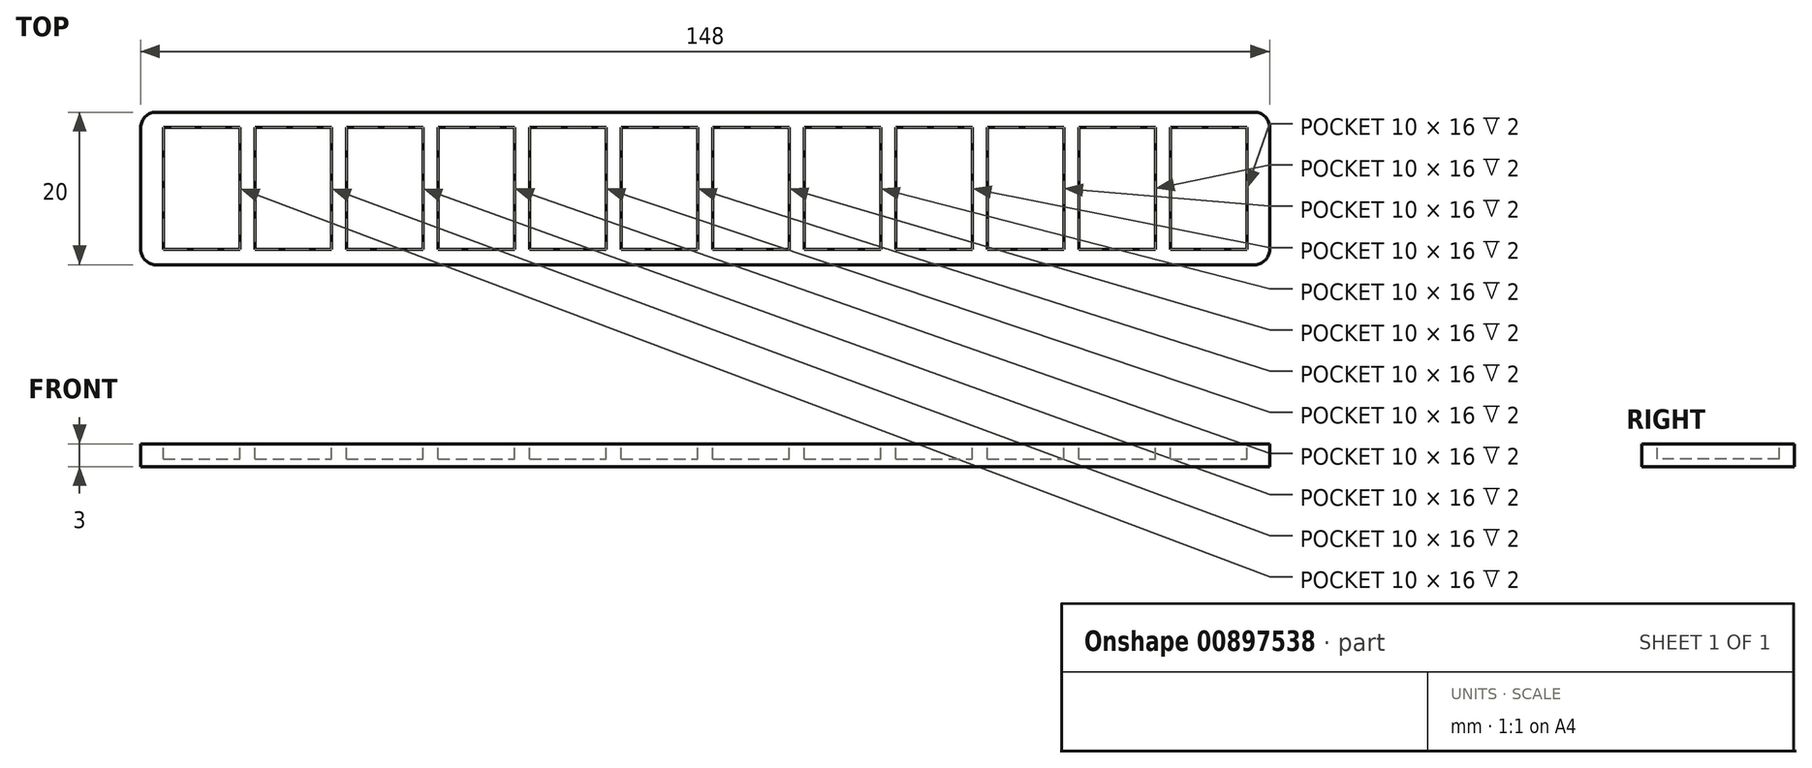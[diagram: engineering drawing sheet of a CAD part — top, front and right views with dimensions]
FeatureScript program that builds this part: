
annotation { "Feature Type Name" : "Feature", "Feature Type Description" : "" }
export const myFeature = defineFeature(function(context is Context, id is Id, definition is map)
    precondition{}
    {
        {
            var Q0;
            Q0=qCreatedBy(makeId("Top.planeOp"),FACE);
            var sketch = newSketch(context, id + "F0", { "sketchPlane" : qUnion([Q0])});
            skLineSegment(sketch, "E0.bottom", {"start": v(-75.02, 10.45) * mm, "end": v(72.98, 10.45) * mm});
            skLineSegment(sketch, "E0.top", {"start": v(-75.02, -9.55) * mm, "end": v(72.98, -9.55) * mm});
            skLineSegment(sketch, "E0.left", {"start": v(-75.02, 10.45) * mm, "end": v(-75.02, -9.55) * mm});
            skLineSegment(sketch, "E0.right", {"start": v(72.98, 10.45) * mm, "end": v(72.98, -9.55) * mm});
            skLineSegment(sketch, "E1", {"start": v(-1.02, 10.45) * mm, "end": v(-1.02, -9.55) * mm, "construction": true});
            skSolve(sketch);
        }
        {
            var Q0;
            Q0 = qSketchRegion(id + "F0", true);
            extrude(context, id + "F1", {"entities" : qUnion([Q0]), "depth" : 3 * mm, "offsetDistance" : 25 * mm});
        }
        {
            var Q0;
            Q0=makeQuery(id+"F1.opExtrude","CAP_FACE",FACE,{"disambiguationData":[OSD([sQuery(id+"F0.wireOp",EDGE,"E0.bottom"),sQuery(id+"F0.wireOp",EDGE,"E0.top"),sQuery(id+"F0.wireOp",EDGE,"E0.left"),sQuery(id+"F0.wireOp",EDGE,"E0.right")])],"isStart":false});
            var sketch = newSketch(context, id + "F2", { "sketchPlane" : qUnion([Q0])});
            skLineSegment(sketch, "E2.bottom", {"start": v(-72.02, 8.45) * mm, "end": v(-62.02, 8.45) * mm});
            skLineSegment(sketch, "E2.top", {"start": v(-72.02, -7.55) * mm, "end": v(-62.02, -7.55) * mm});
            skLineSegment(sketch, "E2.left", {"start": v(-72.02, 8.45) * mm, "end": v(-72.02, -7.55) * mm});
            skLineSegment(sketch, "E2.right", {"start": v(-62.02, 8.45) * mm, "end": v(-62.02, -7.55) * mm});
            skLineSegment(sketch, "E3.1.0.0", {"start": v(-60.02, 8.45) * mm, "end": v(-60.02, -7.55) * mm});
            skLineSegment(sketch, "E3.1.0.1", {"start": v(-60.02, 8.45) * mm, "end": v(-50.02, 8.45) * mm});
            skLineSegment(sketch, "E3.1.0.2", {"start": v(-60.02, -7.55) * mm, "end": v(-50.02, -7.55) * mm});
            skLineSegment(sketch, "E3.1.0.3", {"start": v(-50.02, 8.45) * mm, "end": v(-50.02, -7.55) * mm});
            skLineSegment(sketch, "E3.2.0.0", {"start": v(-48.02, 8.45) * mm, "end": v(-48.02, -7.55) * mm});
            skLineSegment(sketch, "E3.2.0.1", {"start": v(-48.02, 8.45) * mm, "end": v(-38.02, 8.45) * mm});
            skLineSegment(sketch, "E3.2.0.2", {"start": v(-48.02, -7.55) * mm, "end": v(-38.02, -7.55) * mm});
            skLineSegment(sketch, "E3.2.0.3", {"start": v(-38.02, 8.45) * mm, "end": v(-38.02, -7.55) * mm});
            skLineSegment(sketch, "E3.3.0.0", {"start": v(-36.02, 8.45) * mm, "end": v(-36.02, -7.55) * mm});
            skLineSegment(sketch, "E3.3.0.1", {"start": v(-36.02, 8.45) * mm, "end": v(-26.02, 8.45) * mm});
            skLineSegment(sketch, "E3.3.0.2", {"start": v(-36.02, -7.55) * mm, "end": v(-26.02, -7.55) * mm});
            skLineSegment(sketch, "E3.3.0.3", {"start": v(-26.02, 8.45) * mm, "end": v(-26.02, -7.55) * mm});
            skLineSegment(sketch, "E3.4.0.0", {"start": v(-24.02, 8.45) * mm, "end": v(-24.02, -7.55) * mm});
            skLineSegment(sketch, "E3.4.0.1", {"start": v(-24.02, 8.45) * mm, "end": v(-14.02, 8.45) * mm});
            skLineSegment(sketch, "E3.4.0.2", {"start": v(-24.02, -7.55) * mm, "end": v(-14.02, -7.55) * mm});
            skLineSegment(sketch, "E3.4.0.3", {"start": v(-14.02, 8.45) * mm, "end": v(-14.02, -7.55) * mm});
            skLineSegment(sketch, "E3.5.0.0", {"start": v(-12.02, 8.45) * mm, "end": v(-12.02, -7.55) * mm});
            skLineSegment(sketch, "E3.5.0.1", {"start": v(-12.02, 8.45) * mm, "end": v(-2.02, 8.45) * mm});
            skLineSegment(sketch, "E3.5.0.2", {"start": v(-12.02, -7.55) * mm, "end": v(-2.02, -7.55) * mm});
            skLineSegment(sketch, "E3.5.0.3", {"start": v(-2.02, 8.45) * mm, "end": v(-2.02, -7.55) * mm});
            skLineSegment(sketch, "E3.6.0.0", {"start": v(-0.02, 8.45) * mm, "end": v(-0.02, -7.55) * mm});
            skLineSegment(sketch, "E3.6.0.1", {"start": v(-0.02, 8.45) * mm, "end": v(9.98, 8.45) * mm});
            skLineSegment(sketch, "E3.6.0.2", {"start": v(-0.02, -7.55) * mm, "end": v(9.98, -7.55) * mm});
            skLineSegment(sketch, "E3.6.0.3", {"start": v(9.98, 8.45) * mm, "end": v(9.98, -7.55) * mm});
            skLineSegment(sketch, "E3.7.0.0", {"start": v(11.98, 8.45) * mm, "end": v(11.98, -7.55) * mm});
            skLineSegment(sketch, "E3.7.0.1", {"start": v(11.98, 8.45) * mm, "end": v(21.98, 8.45) * mm});
            skLineSegment(sketch, "E3.7.0.2", {"start": v(11.98, -7.55) * mm, "end": v(21.98, -7.55) * mm});
            skLineSegment(sketch, "E3.7.0.3", {"start": v(21.98, 8.45) * mm, "end": v(21.98, -7.55) * mm});
            skLineSegment(sketch, "E3.8.0.0", {"start": v(23.98, 8.45) * mm, "end": v(23.98, -7.55) * mm});
            skLineSegment(sketch, "E3.8.0.1", {"start": v(23.98, 8.45) * mm, "end": v(33.98, 8.45) * mm});
            skLineSegment(sketch, "E3.8.0.2", {"start": v(23.98, -7.55) * mm, "end": v(33.98, -7.55) * mm});
            skLineSegment(sketch, "E3.8.0.3", {"start": v(33.98, 8.45) * mm, "end": v(33.98, -7.55) * mm});
            skLineSegment(sketch, "E3.9.0.0", {"start": v(35.98, 8.45) * mm, "end": v(35.98, -7.55) * mm});
            skLineSegment(sketch, "E3.9.0.1", {"start": v(35.98, 8.45) * mm, "end": v(45.98, 8.45) * mm});
            skLineSegment(sketch, "E3.9.0.2", {"start": v(35.98, -7.55) * mm, "end": v(45.98, -7.55) * mm});
            skLineSegment(sketch, "E3.9.0.3", {"start": v(45.98, 8.45) * mm, "end": v(45.98, -7.55) * mm});
            skLineSegment(sketch, "E3.10.0.0", {"start": v(47.98, 8.45) * mm, "end": v(47.98, -7.55) * mm});
            skLineSegment(sketch, "E3.10.0.1", {"start": v(47.98, 8.45) * mm, "end": v(57.98, 8.45) * mm});
            skLineSegment(sketch, "E3.10.0.2", {"start": v(47.98, -7.55) * mm, "end": v(57.98, -7.55) * mm});
            skLineSegment(sketch, "E3.10.0.3", {"start": v(57.98, 8.45) * mm, "end": v(57.98, -7.55) * mm});
            skLineSegment(sketch, "E3.11.0.0", {"start": v(59.98, 8.45) * mm, "end": v(59.98, -7.55) * mm});
            skLineSegment(sketch, "E3.11.0.1", {"start": v(59.98, 8.45) * mm, "end": v(69.98, 8.45) * mm});
            skLineSegment(sketch, "E3.11.0.2", {"start": v(59.98, -7.55) * mm, "end": v(69.98, -7.55) * mm});
            skLineSegment(sketch, "E3.11.0.3", {"start": v(69.98, 8.45) * mm, "end": v(69.98, -7.55) * mm});
            skLineSegment(sketch, "E3.direction1", {"start": v(-72.02, -7.55) * mm, "end": v(-60.02, -7.55) * mm, "construction": true});
            skSolve(sketch);
        }
        {
            var Q0;
            Q0 = qSketchRegion(id + "F2", true);
            extrude(context, id + "F3", {"entities" : qUnion([Q0]), "operationType" : NewBodyOperationType.REMOVE, "oppositeDirection" : true, "depth" : 2 * mm, "offsetDistance" : 25 * mm});
        }
        {
            var Q0;
            Q0=makeQuery(id+"F1.opExtrude","SWEPT_EDGE",EDGE,{"disambiguationData":[OSD([sQuery(id+"F0.wireOp",EDGE,"E0.top"),sQuery(id+"F0.wireOp",EDGE,"E0.left")])]});
            var Q1;
            Q1=makeQuery(id+"F1.opExtrude","SWEPT_EDGE",EDGE,{"disambiguationData":[OSD([sQuery(id+"F0.wireOp",EDGE,"E0.top"),sQuery(id+"F0.wireOp",EDGE,"E0.right")])]});
            var Q2;
            Q2=makeQuery(id+"F1.opExtrude","SWEPT_EDGE",EDGE,{"disambiguationData":[OSD([sQuery(id+"F0.wireOp",EDGE,"E0.bottom"),sQuery(id+"F0.wireOp",EDGE,"E0.right")])]});
            var Q3;
            Q3=makeQuery(id+"F1.opExtrude","SWEPT_EDGE",EDGE,{"disambiguationData":[OSD([sQuery(id+"F0.wireOp",EDGE,"E0.bottom"),sQuery(id+"F0.wireOp",EDGE,"E0.left")])]});
            var Q4;
            Q4=makeQuery(id+"F3.boolean.opBoolean","COPY",EDGE,{"derivedFrom":makeQuery(id+"F3.opExtrude","CAP_EDGE",EDGE,{"disambiguationData":[OSD([sQuery(id+"F2.wireOp",EDGE,"E2.left")])],"isStart":true})});
            var Q5;
            Q5=makeQuery(id+"F3.boolean.opBoolean","COPY",EDGE,{"derivedFrom":makeQuery(id+"F3.opExtrude","CAP_EDGE",EDGE,{"disambiguationData":[OSD([sQuery(id+"F2.wireOp",EDGE,"E3.1.0.0")])],"isStart":true})});
            var Q6;
            Q6=makeQuery(id+"F3.boolean.opBoolean","COPY",EDGE,{"derivedFrom":makeQuery(id+"F3.opExtrude","CAP_EDGE",EDGE,{"disambiguationData":[OSD([sQuery(id+"F2.wireOp",EDGE,"E3.2.0.0")])],"isStart":true})});
            var Q7;
            Q7=makeQuery(id+"F3.boolean.opBoolean","COPY",EDGE,{"derivedFrom":makeQuery(id+"F3.opExtrude","CAP_EDGE",EDGE,{"disambiguationData":[OSD([sQuery(id+"F2.wireOp",EDGE,"E3.3.0.0")])],"isStart":true})});
            var Q8;
            Q8=makeQuery(id+"F3.boolean.opBoolean","COPY",EDGE,{"derivedFrom":makeQuery(id+"F3.opExtrude","CAP_EDGE",EDGE,{"disambiguationData":[OSD([sQuery(id+"F2.wireOp",EDGE,"E3.4.0.0")])],"isStart":true})});
            var Q9;
            Q9=makeQuery(id+"F3.boolean.opBoolean","COPY",EDGE,{"derivedFrom":makeQuery(id+"F3.opExtrude","CAP_EDGE",EDGE,{"disambiguationData":[OSD([sQuery(id+"F2.wireOp",EDGE,"E3.5.0.0")])],"isStart":true})});
            var Q10;
            Q10=makeQuery(id+"F3.boolean.opBoolean","COPY",EDGE,{"derivedFrom":makeQuery(id+"F3.opExtrude","CAP_EDGE",EDGE,{"disambiguationData":[OSD([sQuery(id+"F2.wireOp",EDGE,"E3.6.0.0")])],"isStart":true})});
            var Q11;
            Q11=makeQuery(id+"F3.boolean.opBoolean","COPY",EDGE,{"derivedFrom":makeQuery(id+"F3.opExtrude","CAP_EDGE",EDGE,{"disambiguationData":[OSD([sQuery(id+"F2.wireOp",EDGE,"E3.7.0.0")])],"isStart":true})});
            var Q12;
            Q12=makeQuery(id+"F3.boolean.opBoolean","COPY",EDGE,{"derivedFrom":makeQuery(id+"F3.opExtrude","CAP_EDGE",EDGE,{"disambiguationData":[OSD([sQuery(id+"F2.wireOp",EDGE,"E3.8.0.0")])],"isStart":true})});
            var Q13;
            Q13=makeQuery(id+"F3.boolean.opBoolean","COPY",EDGE,{"derivedFrom":makeQuery(id+"F3.opExtrude","CAP_EDGE",EDGE,{"disambiguationData":[OSD([sQuery(id+"F2.wireOp",EDGE,"E3.9.0.0")])],"isStart":true})});
            var Q14;
            Q14=makeQuery(id+"F3.boolean.opBoolean","COPY",EDGE,{"derivedFrom":makeQuery(id+"F3.opExtrude","CAP_EDGE",EDGE,{"disambiguationData":[OSD([sQuery(id+"F2.wireOp",EDGE,"E3.10.0.0")])],"isStart":true})});
            var Q15;
            Q15=makeQuery(id+"F3.boolean.opBoolean","COPY",EDGE,{"derivedFrom":makeQuery(id+"F3.opExtrude","CAP_EDGE",EDGE,{"disambiguationData":[OSD([sQuery(id+"F2.wireOp",EDGE,"E3.11.0.0")])],"isStart":true})});
            fillet(context, id + "F4", {"entities" : qUnion([Q0, Q1, Q2, Q3, Q4, Q5, Q6, Q7, Q8, Q9, Q10, Q11, Q12, Q13, Q14, Q15]), "radius" : 2 * mm, "tangentPropagation" : true, "allowEdgeOverflow" : false});
        }
    });
